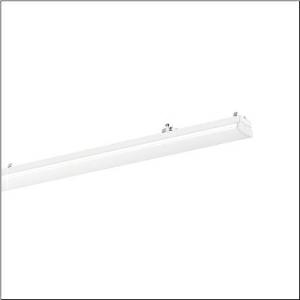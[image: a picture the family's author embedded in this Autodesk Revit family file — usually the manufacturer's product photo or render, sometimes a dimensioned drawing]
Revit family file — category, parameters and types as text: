
# Revit family: licross_21_recessed_opal_ho_52te1ddn4e5m
name_source: partatom
category: Lighting Fixtures
units: mm (PartAtom-declared; Revit-internal decimal feet)

## family parameters
Cut with Voids When Loaded = No
Host = Face
Light Source = No
Part Type = Normal
Room Calculation Point = No
Round Connector Dimension = Use Diameter
Shared = No

## types (1)
- --- (1 x LED, 14560 lm, 84.6 W, 4000K)
    Apparent Load = 85 VA
    CIE Flux Codes = 44 73 91 87 100
    Color Rendering = 80
    Color Temperature = 4000K
    Default Elevation = 1800 mm
    Description = Licross 21 recessed opal HO, luminaire insert, of sheet steel, galvanised, coil coated, white, length: 1.500mm, width: 66mm, height: 67mm, LED rated luminous flux: 14.560lm, light colour: 840, SDCM (Standard Deviation of Colour Matching)MacAdam ≤ 3 SDCM (initial), control gear: DALI 2, with plug, 5-pole, with phase selection, mains connection: 220..240V, AC, 50/60Hz, rated input power: 85W, internal wiring halogen-free, primary optical cover: cover, of PMMA, light emission: direct with ceiling illumination distribution, primary light characteristic: symmetric, protection rating (complete): IP54, insulation class (complete): insulation class I (protective earthing), certification: CE, ENEC, VDE, UKCA, protection symbol: D if used in an environment with non-conductive dust loads with corresponding accessories, impact resistance: IK06, permissible ambient temperature for indoor applications: -25..+30°C, corresponds to IFS (International Featured Standards) requirements for safety and quality in the food industry, reducing of maximum allowable ambient temperature of 5°C with ceiling mounting, LABS conformity tested according to VDMA 24364:2018-05, The light source and the operating device comply with the requirements of the Ecodesign Regulation (EU) 2019/2020 and are replaceable in accordance with this regulation, packaging unit: 1 piece
    Height = 83 mm
    Lamp = 1 x LED
    Lamp Light Flux = 14560 lm
    Lamp Power = 84.6 W
    Lamp count = 1
    Length = 1500 mm
    Luminous efficacy = 172 lm/W
    Manufacturer = Siteco
    ModVariant = No
    Model = 52TE1DDN4E5M
    Mounting Place = Ceiling
    Mounting Type = Pendant
    Number of Poles = 1
    OnlyDefault = Yes
    Power Factor = 1
    Product Name = Licross 21 recessed opal HO
    Product group = luminaire insert | ceiling pendant
    ProductGroupID = 901
    Protection Class = Protection class I
    Protection Degree = IP 54
    RLX_Detail_Level = 1
    RLX_Emergency_Light_Flux = 0 lm
    RLX_Emergency_Type = 0
    RLX_Emergency_Type_DB = No
    RlxData = <blob elided: 27549 chars, md5=d6eae8b6>
    Socket = socket
    Standby Power = 0 W
    System Light Flux = 14560 lm
    System Power = 85 W
    Type Comments = factory setting: luminous flux: 100 % | dim-lin: 254 | 484 mA
    Type Image = l_1313666.jpg
    URL = http://relux.com
    VarID = @adj_076203
    Voltage = 0 V
    Weight = 0.00 kg
    Width = 76 mm

## geometry (parser evidence)
native form markers: Blend x4, Sweep x16
no freeform markers — native parametric forms only
